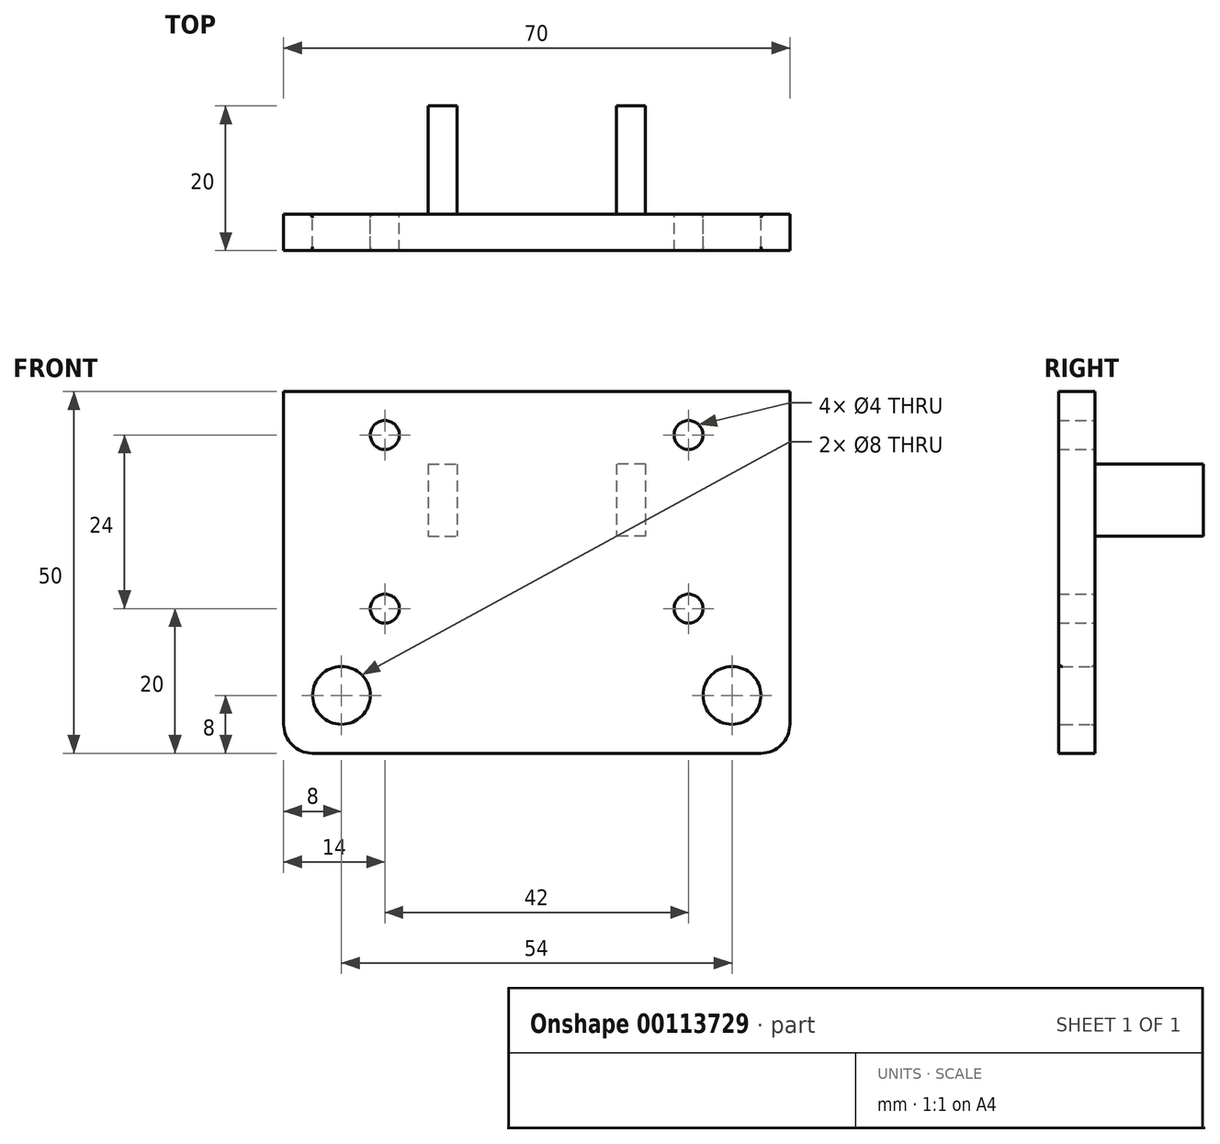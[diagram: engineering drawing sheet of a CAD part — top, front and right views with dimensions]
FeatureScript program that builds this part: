
annotation { "Feature Type Name" : "Feature", "Feature Type Description" : "" }
export const myFeature = defineFeature(function(context is Context, id is Id, definition is map)
    precondition{}
    {
        {
            var Q0;
            Q0=qCreatedBy(makeId("Front.planeOp"),FACE);
            var sketch = newSketch(context, id + "F0", { "sketchPlane" : qUnion([Q0])});
            skLineSegment(sketch, "E0.bottom", {"start": v(-35, 25) * mm, "end": v(35, 25) * mm});
            skLineSegment(sketch, "E0.top", {"start": v(-35, -25) * mm, "end": v(35, -25) * mm});
            skLineSegment(sketch, "E0.left", {"start": v(-35, 25) * mm, "end": v(-35, -25) * mm});
            skLineSegment(sketch, "E0.right", {"start": v(35, 25) * mm, "end": v(35, -25) * mm});
            skLineSegment(sketch, "E1", {"start": v(0, 25) * mm, "end": v(0, -25) * mm, "construction": true});
            skCircle(sketch, "E2", {"center": v(-21, 19) * mm, "radius": 2 * mm});
            skCircle(sketch, "E3.0.1.0", {"center": v(-21, -5) * mm, "radius": 2 * mm});
            skCircle(sketch, "E3.1.0.0", {"center": v(21, 19) * mm, "radius": 2 * mm});
            skCircle(sketch, "E3.1.1.0", {"center": v(21, -5) * mm, "radius": 2 * mm});
            skLineSegment(sketch, "E3.direction1", {"start": v(-21, 19) * mm, "end": v(21, 19) * mm, "construction": true});
            skLineSegment(sketch, "E3.direction2", {"start": v(-21, 19) * mm, "end": v(-21, -5) * mm, "construction": true});
            skCircle(sketch, "E4", {"center": v(-27, -17) * mm, "radius": 4 * mm});
            skCircle(sketch, "E5.MirrorC", {"center": v(27, -17) * mm, "radius": 4 * mm});
            skSolve(sketch);
        }
        {
            var Q0;
            Q0=makeQuery(id+"F0.imprint","IMPRINT",FACE,{"disambiguationData":[TD([[makeQuery(id+"F0.imprint","IMPRINT",EDGE,{"derivedFrom":sQuery(id+"F0.wireOp",EDGE,"E0.bottom")}),-1.0]])]});
            extrude(context, id + "F1", {"entities" : qUnion([Q0]), "depth" : 5 * mm});
        }
        {
            var Q0;
            Q0=makeQuery(id+"F1.opExtrude","SWEPT_EDGE",EDGE,{"disambiguationData":[OSD([sQuery(id+"F0.wireOp",EDGE,"E0.top"),sQuery(id+"F0.wireOp",EDGE,"E0.right")])]});
            var Q1;
            Q1=makeQuery(id+"F1.opExtrude","SWEPT_EDGE",EDGE,{"disambiguationData":[OSD([sQuery(id+"F0.wireOp",EDGE,"E0.top"),sQuery(id+"F0.wireOp",EDGE,"E0.left")])]});
            fillet(context, id + "F2", {"entities" : qUnion([Q0, Q1]), "radius" : 4 * mm, "tangentPropagation" : true, "allowEdgeOverflow" : false});
        }
        {
            var Q0;
            Q0=makeQuery(id+"F1.opExtrude","CAP_EDGE",EDGE,{"disambiguationData":[OSD([sQuery(id+"F0.wireOp",EDGE,"E4")])],"isStart":false});
            var Q1;
            Q1=makeQuery(id+"F1.opExtrude","CAP_EDGE",EDGE,{"disambiguationData":[OSD([sQuery(id+"F0.wireOp",EDGE,"E5.MirrorC")])],"isStart":false});
            var Q2;
            Q2=makeQuery(id+"F1.opExtrude","CAP_EDGE",EDGE,{"disambiguationData":[OSD([sQuery(id+"F0.wireOp",EDGE,"E4")])],"isStart":true});
            var Q3;
            Q3=makeQuery(id+"F1.opExtrude","CAP_EDGE",EDGE,{"disambiguationData":[OSD([sQuery(id+"F0.wireOp",EDGE,"E5.MirrorC")])],"isStart":true});
            fillet(context, id + "F3", {"entities" : qUnion([Q0, Q1, Q2, Q3]), "radius" : 0.5 * mm, "tangentPropagation" : true, "allowEdgeOverflow" : false});
        }
        {
            var Q0;
            Q0=makeQuery(id+"F1.opExtrude","CAP_FACE",FACE,{"disambiguationData":[OSD([sQuery(id+"F0.wireOp",EDGE,"E0.bottom"),sQuery(id+"F0.wireOp",EDGE,"E0.top"),sQuery(id+"F0.wireOp",EDGE,"E0.left"),sQuery(id+"F0.wireOp",EDGE,"E0.right"),sQuery(id+"F0.wireOp",EDGE,"E2"),sQuery(id+"F0.wireOp",EDGE,"E3.0.1.0"),sQuery(id+"F0.wireOp",EDGE,"E3.1.0.0"),sQuery(id+"F0.wireOp",EDGE,"E3.1.1.0"),sQuery(id+"F0.wireOp",EDGE,"E4"),sQuery(id+"F0.wireOp",EDGE,"E5.MirrorC")])],"isStart":true});
            var sketch = newSketch(context, id + "F4", { "sketchPlane" : qUnion([Q0])});
            skLineSegment(sketch, "E6", {"start": v(0, 25) * mm, "end": v(0, -25) * mm, "construction": true});
            skLineSegment(sketch, "E7.bottom", {"start": v(-15, 15) * mm, "end": v(-11, 15) * mm});
            skLineSegment(sketch, "E7.top", {"start": v(-15, 5) * mm, "end": v(-11, 5) * mm});
            skLineSegment(sketch, "E7.left", {"start": v(-15, 15) * mm, "end": v(-15, 5) * mm});
            skLineSegment(sketch, "E7.right", {"start": v(-11, 15) * mm, "end": v(-11, 5) * mm});
            skLineSegment(sketch, "E8.MirrorCS", {"start": v(11, 15) * mm, "end": v(11, 5) * mm});
            skLineSegment(sketch, "E9.MirrorCS", {"start": v(15, 15) * mm, "end": v(15, 5) * mm});
            skLineSegment(sketch, "E10.MirrorCS", {"start": v(15, 5) * mm, "end": v(11, 5) * mm});
            skLineSegment(sketch, "E11.MirrorCS", {"start": v(15, 15) * mm, "end": v(11, 15) * mm});
            skSolve(sketch);
        }
        {
            var Q0;
            Q0=makeQuery(id+"F4.imprint","IMPRINT",FACE,{"disambiguationData":[TD([[makeQuery(id+"F4.imprint","IMPRINT",EDGE,{"derivedFrom":sQuery(id+"F4.wireOp",EDGE,"E7.bottom")}),-1.0]])]});
            var Q1;
            Q1=makeQuery(id+"F4.imprint","IMPRINT",FACE,{"disambiguationData":[TD([[makeQuery(id+"F4.imprint","IMPRINT",EDGE,{"derivedFrom":sQuery(id+"F4.wireOp",EDGE,"E8.MirrorCS")}),1.0]])]});
            extrude(context, id + "F5", {"entities" : qUnion([Q0, Q1]), "operationType" : NewBodyOperationType.ADD, "depth" : 15 * mm});
        }
    });
